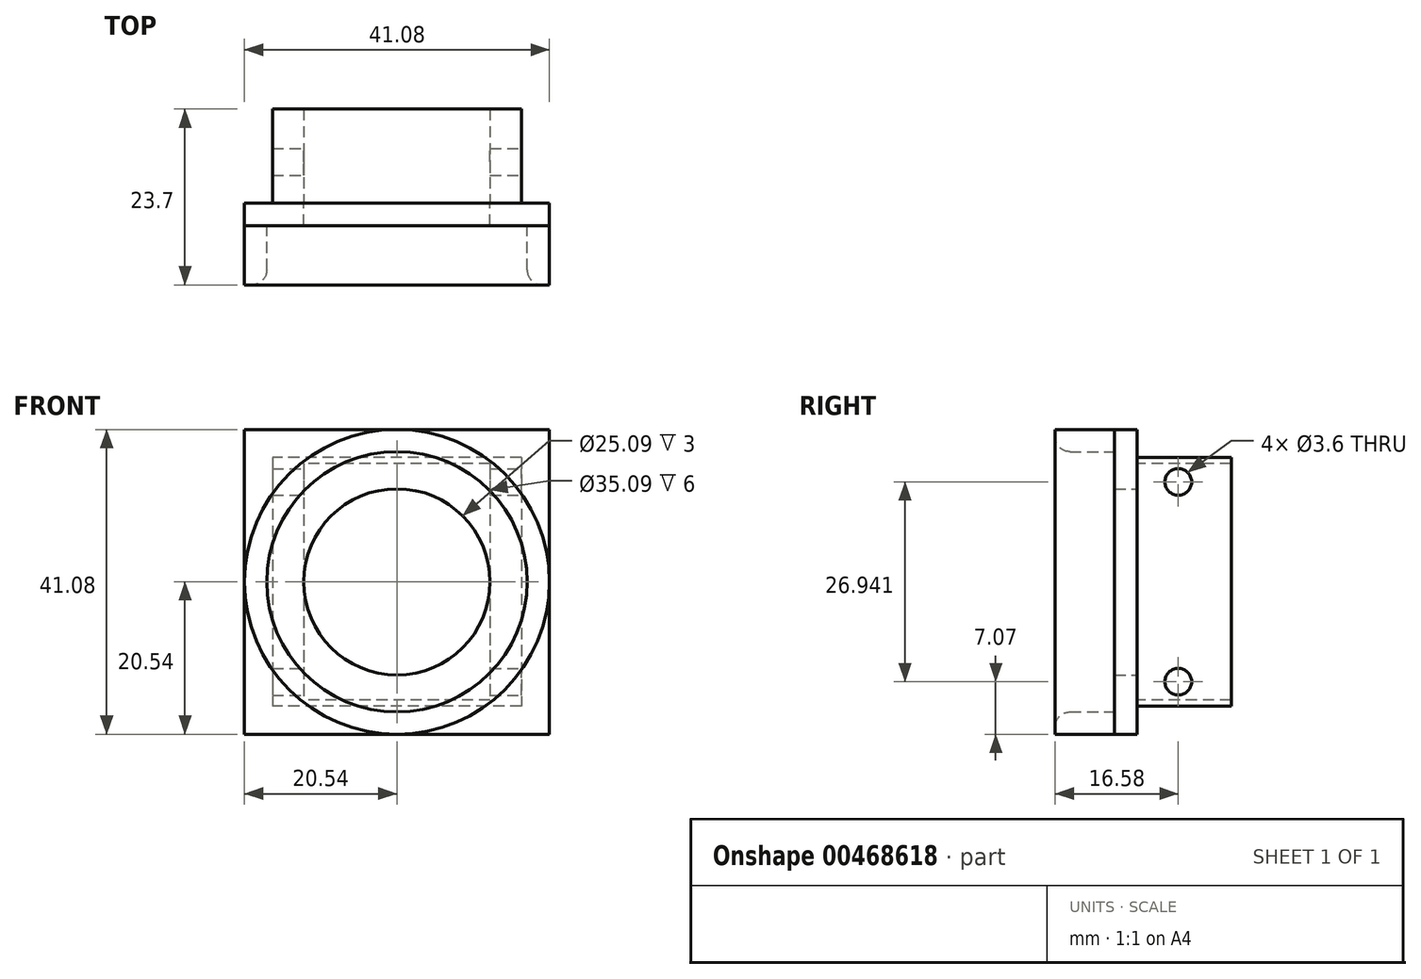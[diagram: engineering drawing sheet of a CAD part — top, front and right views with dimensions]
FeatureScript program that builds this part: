
annotation { "Feature Type Name" : "Feature", "Feature Type Description" : "" }
export const myFeature = defineFeature(function(context is Context, id is Id, definition is map)
    precondition{}
    {
        {
            var Q0;
            Q0=qCreatedBy(makeId("Front.planeOp"),FACE);
            var sketch = newSketch(context, id + "F0", { "sketchPlane" : qUnion([Q0])});
            skCircle(sketch, "E0", {"center": v(0, 0) * mm, "radius": 17.54 * mm});
            skLineSegment(sketch, "E1.bottom", {"start": v(-20.54, 20.54) * mm, "end": v(20.54, 20.54) * mm});
            skLineSegment(sketch, "E1.top", {"start": v(-20.54, -20.54) * mm, "end": v(20.54, -20.54) * mm});
            skLineSegment(sketch, "E1.left", {"start": v(-20.54, 20.54) * mm, "end": v(-20.54, -20.54) * mm});
            skLineSegment(sketch, "E1.right", {"start": v(20.54, 20.54) * mm, "end": v(20.54, -20.54) * mm});
            skPoint(sketch, "E2.centerSnap1", {"position": v(-20.54, 0) * mm});
            skCircle(sketch, "E3", {"center": v(0, 0) * mm, "radius": 12.54 * mm});
            skCircle(sketch, "E4", {"center": v(0, 0) * mm, "radius": 20.54 * mm});
            skSolve(sketch);
        }
        {
            var Q0;
            Q0=makeQuery(id+"F0.imprint","IMPRINT",FACE,{"disambiguationData":[TD([[makeQuery(id+"F0.imprint","IMPRINT",EDGE,{"derivedFrom":sQuery(id+"F0.wireOp",EDGE,"E0")}),-1.0]])]});
            var Q1;
            {var subQ1=sQuery(id+"F0.wireOp",EDGE,"E1.right");Q1=makeQuery(id+"F0.imprint","IMPRINT",FACE,{"disambiguationData":[TD([[makeQuery(id+"F0.imprint","IMPRINT",EDGE,{"derivedFrom":subQ1}),1.0]])]});}
            var Q2;
            {var subQ1=sQuery(id+"F0.wireOp",EDGE,"E1.left");Q2=makeQuery(id+"F0.imprint","IMPRINT",FACE,{"disambiguationData":[TD([[makeQuery(id+"F0.imprint","IMPRINT",EDGE,{"derivedFrom":subQ1}),-1.0]])]});}
            var Q3;
            {var subQ1=sQuery(id+"F0.wireOp",EDGE,"E1.bottom");var subQ3=sQuery(id+"F0.wireOp",EDGE,"E4");var subQ4=makeQuery(id+"F0.imprint","INTERSECT",VERTEX,{"derivedFrom":[subQ1,subQ3]});Q3=makeQuery(id+"F0.imprint","IMPRINT",FACE,{"disambiguationData":[TD([[makeQuery(id+"F0.imprint","IMPRINT",EDGE,{"disambiguationData":[TD([[subQ4,-1.0]])],"derivedFrom":subQ3}),-1.0]])]});}
            var Q4;
            {var subQ0=sQuery(id+"F0.wireOp",EDGE,"E4");var subQ1=sQuery(id+"F0.wireOp",EDGE,"E1.left");var subQ2=makeQuery(id+"F0.imprint","INTERSECT",VERTEX,{"disambiguationData":[OD(0.0)],"derivedFrom":[subQ1,subQ0]});Q4=makeQuery(id+"F0.imprint","IMPRINT",FACE,{"disambiguationData":[TD([[makeQuery(id+"F0.imprint","IMPRINT",EDGE,{"disambiguationData":[TD([[subQ2,-1.0]])],"derivedFrom":subQ1}),-1.0]])]});}
            var Q5;
            {var subQ0=sQuery(id+"F0.wireOp",EDGE,"E4");var subQ1=sQuery(id+"F0.wireOp",EDGE,"E1.right");var subQ2=makeQuery(id+"F0.imprint","INTERSECT",VERTEX,{"disambiguationData":[OD(0.0)],"derivedFrom":[subQ1,subQ0]});Q5=makeQuery(id+"F0.imprint","IMPRINT",FACE,{"disambiguationData":[TD([[makeQuery(id+"F0.imprint","IMPRINT",EDGE,{"disambiguationData":[TD([[subQ2,-1.0]])],"derivedFrom":subQ1}),1.0]])]});}
            var Q6;
            {var subQ1=sQuery(id+"F0.wireOp",EDGE,"E1.bottom");var subQ3=sQuery(id+"F0.wireOp",EDGE,"E4");var subQ4=makeQuery(id+"F0.imprint","INTERSECT",VERTEX,{"derivedFrom":[subQ1,subQ3]});Q6=makeQuery(id+"F0.imprint","IMPRINT",FACE,{"disambiguationData":[TD([[makeQuery(id+"F0.imprint","IMPRINT",EDGE,{"disambiguationData":[TD([[subQ4,1.0]])],"derivedFrom":subQ3}),-1.0]])]});}
            var Q7;
            {var subQ1=sQuery(id+"F0.wireOp",EDGE,"E1.top");var subQ3=sQuery(id+"F0.wireOp",EDGE,"E4");var subQ4=makeQuery(id+"F0.imprint","INTERSECT",VERTEX,{"derivedFrom":[subQ1,subQ3]});Q7=makeQuery(id+"F0.imprint","IMPRINT",FACE,{"disambiguationData":[TD([[makeQuery(id+"F0.imprint","IMPRINT",EDGE,{"disambiguationData":[TD([[subQ4,-1.0]])],"derivedFrom":subQ3}),-1.0]])]});}
            var Q8;
            {var subQ1=sQuery(id+"F0.wireOp",EDGE,"E1.top");var subQ3=sQuery(id+"F0.wireOp",EDGE,"E4");var subQ4=makeQuery(id+"F0.imprint","INTERSECT",VERTEX,{"derivedFrom":[subQ1,subQ3]});Q8=makeQuery(id+"F0.imprint","IMPRINT",FACE,{"disambiguationData":[TD([[makeQuery(id+"F0.imprint","IMPRINT",EDGE,{"disambiguationData":[TD([[subQ4,1.0]])],"derivedFrom":subQ3}),-1.0]])]});}
            extrude(context, id + "F1", {"entities" : qUnion([Q0, Q1, Q2, Q3, Q4, Q5, Q6, Q7, Q8]), "depth" : 3 * mm, "offsetDistance" : 25 * mm});
        }
        {
            var Q0;
            Q0=makeQuery(id+"F0.imprint","IMPRINT",FACE,{"disambiguationData":[TD([[makeQuery(id+"F0.imprint","IMPRINT",EDGE,{"derivedFrom":sQuery(id+"F0.wireOp",EDGE,"E0")}),1.0]])]});
            extrude(context, id + "F2", {"entities" : qUnion([Q0]), "operationType" : NewBodyOperationType.ADD, "depth" : 3 * mm, "offsetDistance" : 25 * mm});
        }
        {
            var Q0;
            Q0=makeQuery(id+"F0.imprint","IMPRINT",FACE,{"disambiguationData":[TD([[makeQuery(id+"F0.imprint","IMPRINT",EDGE,{"derivedFrom":sQuery(id+"F0.wireOp",EDGE,"E0")}),-1.0]])]});
            var Q1;
            {var subQ0=sQuery(id+"F0.wireOp",EDGE,"E4");var subQ1=sQuery(id+"F0.wireOp",EDGE,"E1.left");var subQ2=makeQuery(id+"F0.imprint","INTERSECT",VERTEX,{"disambiguationData":[OD(0.0)],"derivedFrom":[subQ1,subQ0]});Q1=makeQuery(id+"F0.imprint","IMPRINT",FACE,{"disambiguationData":[TD([[makeQuery(id+"F0.imprint","IMPRINT",EDGE,{"disambiguationData":[TD([[subQ2,-1.0]])],"derivedFrom":subQ1}),-1.0]])]});}
            var Q2;
            {var subQ0=sQuery(id+"F0.wireOp",EDGE,"E4");var subQ1=sQuery(id+"F0.wireOp",EDGE,"E1.right");var subQ2=makeQuery(id+"F0.imprint","INTERSECT",VERTEX,{"disambiguationData":[OD(0.0)],"derivedFrom":[subQ1,subQ0]});Q2=makeQuery(id+"F0.imprint","IMPRINT",FACE,{"disambiguationData":[TD([[makeQuery(id+"F0.imprint","IMPRINT",EDGE,{"disambiguationData":[TD([[subQ2,-1.0]])],"derivedFrom":subQ1}),1.0]])]});}
            extrude(context, id + "F3", {"entities" : qUnion([Q0, Q1, Q2]), "operationType" : NewBodyOperationType.ADD, "depth" : 11 * mm, "offsetDistance" : 25 * mm});
        }
        {
            var Q0;
            Q0=makeQuery(id+"F3.opExtrude","CAP_EDGE",EDGE,{"disambiguationData":[OSD([sQuery(id+"F0.wireOp",EDGE,"E0")])],"isStart":false});
            fillet(context, id + "F4", {"entities" : qUnion([Q0]), "radius" : 2 * mm, "tangentPropagation" : true, "allowEdgeOverflow" : false});
        }
        {
            var Q0;
            Q0=qCreatedBy(makeId("Front.planeOp"),FACE);
            var sketch = newSketch(context, id + "F5", { "sketchPlane" : qUnion([Q0])});
            skLineSegment(sketch, "E5.bottom", {"start": v(16.76, 16.76) * mm, "end": v(-16.76, 16.76) * mm});
            skLineSegment(sketch, "E5.top", {"start": v(16.76, -16.76) * mm, "end": v(-16.76, -16.76) * mm});
            skLineSegment(sketch, "E5.left", {"start": v(16.76, 16.76) * mm, "end": v(16.76, -16.76) * mm});
            skLineSegment(sketch, "E5.right", {"start": v(-16.76, 16.76) * mm, "end": v(-16.76, -16.76) * mm});
            skPoint(sketch, "E5.middle", {"position": v(0, 0) * mm});
            skLineSegment(sketch, "E6.bottom", {"start": v(15.96, 15.96) * mm, "end": v(-15.96, 15.96) * mm});
            skLineSegment(sketch, "E6.top", {"start": v(15.96, -15.96) * mm, "end": v(-15.96, -15.96) * mm});
            skLineSegment(sketch, "E6.left", {"start": v(15.96, 15.96) * mm, "end": v(15.96, -15.96) * mm});
            skLineSegment(sketch, "E6.right", {"start": v(-15.96, 15.96) * mm, "end": v(-15.96, -15.96) * mm});
            skLineSegment(sketch, "E7", {"start": v(12.54, 15.96) * mm, "end": v(12.54, -15.96) * mm});
            skLineSegment(sketch, "E8", {"start": v(-12.54, 15.96) * mm, "end": v(-12.54, -15.96) * mm});
            skSolve(sketch);
        }
        {
            var Q0;
            Q0=makeQuery(id+"F5.imprint","IMPRINT",FACE,{"disambiguationData":[TD([[makeQuery(id+"F5.imprint","IMPRINT",EDGE,{"derivedFrom":sQuery(id+"F5.wireOp",EDGE,"E5.bottom")}),1.0]])]});
            var Q1;
            {var subQ2=sQuery(id+"F5.wireOp",EDGE,"E6.left");Q1=makeQuery(id+"F5.imprint","IMPRINT",FACE,{"disambiguationData":[TD([[makeQuery(id+"F5.imprint","IMPRINT",EDGE,{"derivedFrom":subQ2}),-1.0]])]});}
            var Q2;
            {var subQ0=sQuery(id+"F5.wireOp",EDGE,"E6.right");Q2=makeQuery(id+"F5.imprint","IMPRINT",FACE,{"disambiguationData":[TD([[makeQuery(id+"F5.imprint","IMPRINT",EDGE,{"derivedFrom":subQ0}),1.0]])]});}
            extrude(context, id + "F6", {"entities" : qUnion([Q0, Q1, Q2]), "operationType" : NewBodyOperationType.ADD, "oppositeDirection" : true, "depth" : 12.7 * mm, "offsetDistance" : 25 * mm});
        }
        {
            var Q0;
            Q0=makeQuery(id+"F6.opExtrude","SWEPT_FACE",FACE,{"disambiguationData":[OSD([sQuery(id+"F5.wireOp",EDGE,"E5.left")])]});
            var sketch = newSketch(context, id + "F7", { "sketchPlane" : qUnion([Q0])});
            skCircle(sketch, "E9", {"center": v(19.05, 0) * mm, "radius": 19.05 * mm, "construction": true});
            skLineSegment(sketch, "E10.bottom", {"start": v(5.58, 13.47) * mm, "end": v(32.52, 13.47) * mm, "construction": true});
            skLineSegment(sketch, "E10.top", {"start": v(5.58, -13.47) * mm, "end": v(32.52, -13.47) * mm, "construction": true});
            skLineSegment(sketch, "E10.left", {"start": v(5.58, 13.47) * mm, "end": v(5.58, -13.47) * mm, "construction": true});
            skLineSegment(sketch, "E10.right", {"start": v(32.52, 13.47) * mm, "end": v(32.52, -13.47) * mm, "construction": true});
            skCircle(sketch, "E11", {"center": v(5.58, 13.47) * mm, "radius": 1.8 * mm});
            skCircle(sketch, "E12", {"center": v(5.58, -13.47) * mm, "radius": 1.8 * mm});
            skSolve(sketch);
        }
        {
            var Q0;
            Q0=makeQuery(id+"F7.imprint","IMPRINT",FACE,{"disambiguationData":[TD([[makeQuery(id+"F7.imprint","IMPRINT",EDGE,{"derivedFrom":sQuery(id+"F7.wireOp",EDGE,"E11")}),1.0]])]});
            var Q1;
            Q1=makeQuery(id+"F7.imprint","IMPRINT",FACE,{"disambiguationData":[TD([[makeQuery(id+"F7.imprint","IMPRINT",EDGE,{"derivedFrom":sQuery(id+"F7.wireOp",EDGE,"E12")}),1.0]])]});
            extrude(context, id + "F8", {"entities" : qUnion([Q0, Q1]), "operationType" : NewBodyOperationType.REMOVE, "endBound" : BoundingType.THROUGH_ALL, "oppositeDirection" : true, "depth" : 25 * mm, "offsetDistance" : 25 * mm});
        }
    });
